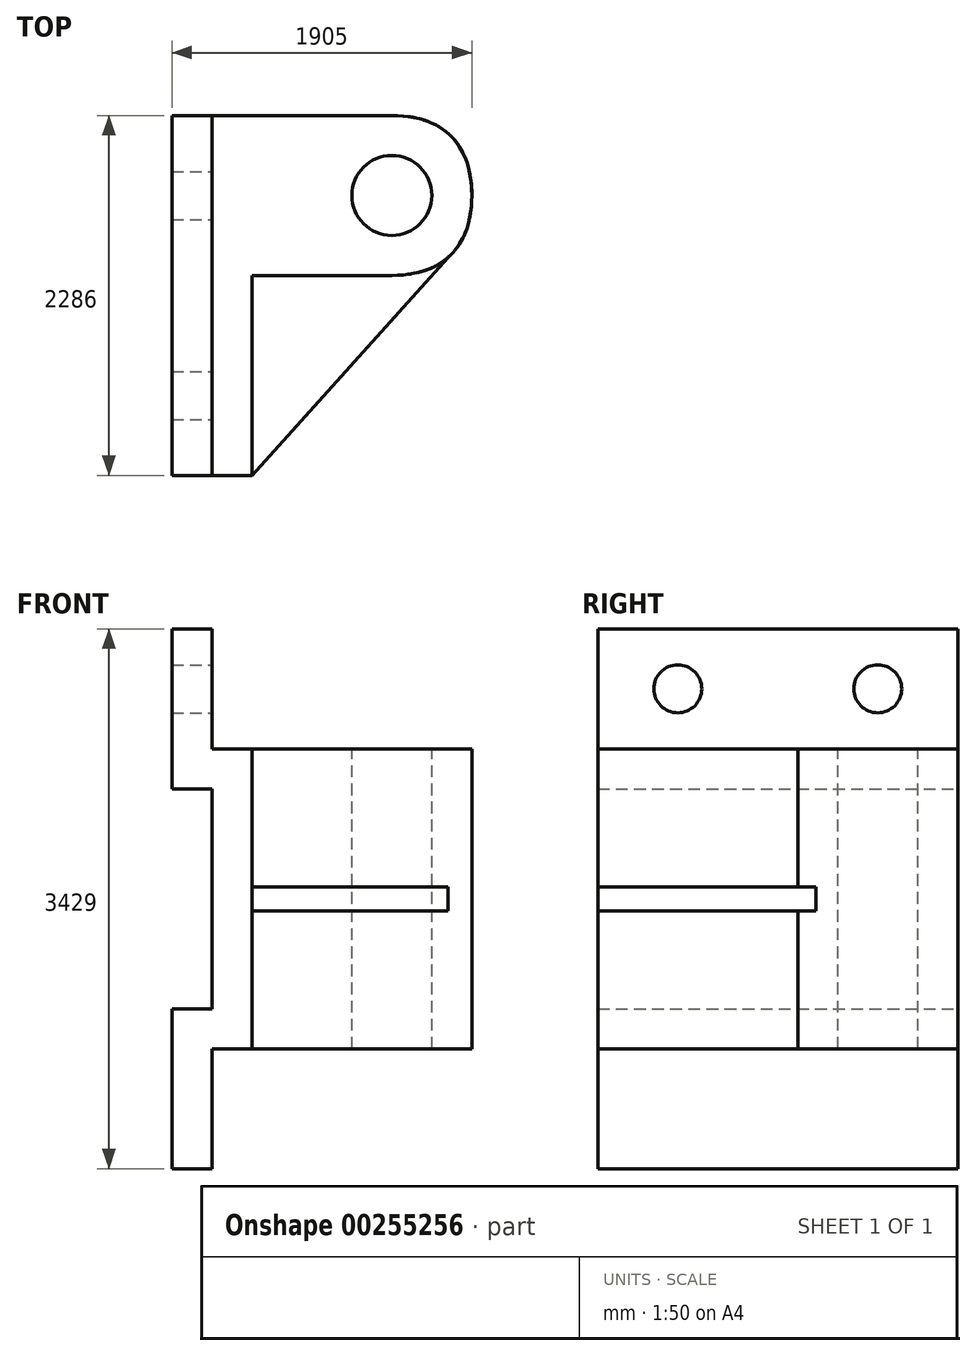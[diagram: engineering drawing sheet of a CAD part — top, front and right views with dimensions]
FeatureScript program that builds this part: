
annotation { "Feature Type Name" : "Feature", "Feature Type Description" : "" }
export const myFeature = defineFeature(function(context is Context, id is Id, definition is map)
    precondition{}
    {
        {
            var Q0;
            Q0=qCreatedBy(makeId("Front.planeOp"),FACE);
            var sketch = newSketch(context, id + "F0", { "sketchPlane" : qUnion([Q0])});
            skLineSegment(sketch, "E0.bottom", {"start": v(0, 0) * mm, "end": v(254, 0) * mm});
            skLineSegment(sketch, "E0.top", {"start": v(0, 1270) * mm, "end": v(254, 1270) * mm});
            skLineSegment(sketch, "E0.left", {"start": v(0, 0) * mm, "end": v(0, 1270) * mm});
            skLineSegment(sketch, "E0.right", {"start": v(254, 0) * mm, "end": v(254, 1270) * mm});
            skLineSegment(sketch, "E1", {"start": v(254, 0) * mm, "end": v(254, 762) * mm});
            skLineSegment(sketch, "E2.bottom", {"start": v(254, 762) * mm, "end": v(508, 762) * mm});
            skLineSegment(sketch, "E2.top", {"start": v(254, 2667) * mm, "end": v(508, 2667) * mm});
            skLineSegment(sketch, "E2.left", {"start": v(254, 762) * mm, "end": v(254, 2667) * mm});
            skLineSegment(sketch, "E2.right", {"start": v(508, 762) * mm, "end": v(508, 2667) * mm});
            skLineSegment(sketch, "E3", {"start": v(508, 1714.5) * mm, "end": v(749.87, 1714.5) * mm});
            skPoint(sketch, "E3.endSnap0", {"position": v(508, 1714.5) * mm});
            skLineSegment(sketch, "E4.MirrorCS", {"start": v(0, 2159) * mm, "end": v(254, 2159) * mm});
            skLineSegment(sketch, "E5.MirrorCS", {"start": v(0, 3429) * mm, "end": v(0, 2159) * mm});
            skLineSegment(sketch, "E6.MirrorCS", {"start": v(0, 3429) * mm, "end": v(254, 3429) * mm});
            skLineSegment(sketch, "E7.MirrorCS", {"start": v(254, 3429) * mm, "end": v(254, 2667) * mm});
            skSolve(sketch);
        }
        {
            var Q0;
            {var subQ0=sQuery(id+"F0.wireOp",EDGE,"E4.MirrorCS");Q0=makeQuery(id+"F0.imprint","IMPRINT",FACE,{"disambiguationData":[TD([[makeQuery(id+"F0.imprint","IMPRINT",EDGE,{"derivedFrom":subQ0}),1.0]])]});}
            var Q1;
            {var subQ3=sQuery(id+"F0.wireOp",EDGE,"E2.bottom");Q1=makeQuery(id+"F0.imprint","IMPRINT",FACE,{"disambiguationData":[TD([[makeQuery(id+"F0.imprint","IMPRINT",EDGE,{"derivedFrom":subQ3}),1.0]])]});}
            var Q2;
            Q2=makeQuery(id+"F0.imprint","IMPRINT",FACE,{"disambiguationData":[TD([[makeQuery(id+"F0.imprint","IMPRINT",EDGE,{"derivedFrom":sQuery(id+"F0.wireOp",EDGE,"E0.bottom")}),1.0]])]});
            extrude(context, id + "F1", {"entities" : qUnion([Q0, Q1, Q2]), "depth" : 2286 * mm});
        }
        {
            var Q0;
            Q0=makeQuery(id+"F1.opExtrude","SWEPT_FACE",FACE,{"disambiguationData":[OSD([sQuery(id+"F0.wireOp",EDGE,"E7.MirrorCS")])]});
            var sketch = newSketch(context, id + "F2", { "sketchPlane" : qUnion([Q0])});
            skLineSegment(sketch, "E8.bottom", {"start": v(-2286, 3429) * mm, "end": v(-1778, 3429) * mm});
            skLineSegment(sketch, "E8.top", {"start": v(-2286, 3048) * mm, "end": v(-1778, 3048) * mm});
            skLineSegment(sketch, "E8.left", {"start": v(-2286, 3429) * mm, "end": v(-2286, 3048) * mm});
            skLineSegment(sketch, "E8.right", {"start": v(-1778, 3429) * mm, "end": v(-1778, 3048) * mm});
            skCircle(sketch, "E9", {"center": v(-1778, 3048) * mm, "radius": 152.4 * mm});
            skLineSegment(sketch, "E10", {"start": v(-1778, 3048) * mm, "end": v(-508, 3048) * mm});
            skCircle(sketch, "E11", {"center": v(-508, 3048) * mm, "radius": 152.4 * mm});
            skLineSegment(sketch, "E12.0.0", {"start": v(0, 762) * mm, "end": v(0, 2667) * mm});
            skLineSegment(sketch, "E12.0.1", {"start": v(0, 2667) * mm, "end": v(-2286, 2667) * mm});
            skLineSegment(sketch, "E12.0.2", {"start": v(-2286, 2667) * mm, "end": v(-2286, 762) * mm});
            skLineSegment(sketch, "E12.0.3", {"start": v(-2286, 762) * mm, "end": v(0, 762) * mm});
            skLineSegment(sketch, "E13", {"start": v(-2286, 1714.5) * mm, "end": v(-1856.1, 1714.5) * mm});
            skCircle(sketch, "E14.MirrorC", {"center": v(-508, 381) * mm, "radius": 152.4 * mm});
            skCircle(sketch, "E15.MirrorC", {"center": v(-1778, 381) * mm, "radius": 152.4 * mm});
            skSolve(sketch);
        }
        {
            var Q0;
            {var subQ0=sQuery(id+"F2.wireOp",EDGE,"E10");var subQ3=sQuery(id+"F2.wireOp",EDGE,"E9");var subQ5=makeQuery(id+"F2.imprint","INTERSECT",VERTEX,{"derivedFrom":[subQ3,subQ0]});Q0=makeQuery(id+"F2.imprint","IMPRINT",FACE,{"disambiguationData":[TD([[makeQuery(id+"F2.imprint","IMPRINT",EDGE,{"disambiguationData":[TD([[subQ5,1.0]])],"derivedFrom":subQ3}),1.0]])]});}
            var Q1;
            {var subQ0=sQuery(id+"F2.wireOp",EDGE,"E10");var subQ3=sQuery(id+"F2.wireOp",EDGE,"E9");var subQ5=makeQuery(id+"F2.imprint","INTERSECT",VERTEX,{"derivedFrom":[subQ3,subQ0]});Q1=makeQuery(id+"F2.imprint","IMPRINT",FACE,{"disambiguationData":[TD([[makeQuery(id+"F2.imprint","IMPRINT",EDGE,{"disambiguationData":[TD([[subQ5,-1.0]])],"derivedFrom":subQ3}),1.0]])]});}
            var Q2;
            {var subQ1=sQuery(id+"F2.wireOp",EDGE,"E8.top");var subQ3=sQuery(id+"F2.wireOp",EDGE,"E9");var subQ4=makeQuery(id+"F2.imprint","INTERSECT",VERTEX,{"derivedFrom":[subQ1,subQ3]});Q2=makeQuery(id+"F2.imprint","IMPRINT",FACE,{"disambiguationData":[TD([[makeQuery(id+"F2.imprint","IMPRINT",EDGE,{"disambiguationData":[TD([[subQ4,1.0]])],"derivedFrom":subQ3}),1.0]])]});}
            var Q3;
            Q3=makeQuery(id+"F2.imprint","IMPRINT",FACE,{"disambiguationData":[TD([[makeQuery(id+"F2.imprint","IMPRINT",EDGE,{"derivedFrom":sQuery(id+"F2.wireOp",EDGE,"E11")}),1.0]])]});
            var Q4;
            Q4=makeQuery(id+"F2.imprint","IMPRINT",FACE,{"disambiguationData":[TD([[makeQuery(id+"F2.imprint","IMPRINT",EDGE,{"derivedFrom":sQuery(id+"F2.wireOp",EDGE,"E15.MirrorC")}),-1.0]])]});
            var Q5;
            Q5=makeQuery(id+"F2.imprint","IMPRINT",FACE,{"disambiguationData":[TD([[makeQuery(id+"F2.imprint","IMPRINT",EDGE,{"derivedFrom":sQuery(id+"F2.wireOp",EDGE,"E14.MirrorC")}),-1.0]])]});
            extrude(context, id + "F3", {"entities" : qUnion([Q0, Q1, Q2, Q3, Q4, Q5]), "operationType" : NewBodyOperationType.REMOVE, "oppositeDirection" : true, "depth" : 254 * mm});
        }
        {
            var Q0;
            Q0=makeQuery(id+"F1.opExtrude","SWEPT_FACE",FACE,{"disambiguationData":[OSD([sQuery(id+"F0.wireOp",EDGE,"E2.right")])]});
            var sketch = newSketch(context, id + "F4", { "sketchPlane" : qUnion([Q0])});
            skLineSegment(sketch, "E16.bottom", {"start": v(0, 2667) * mm, "end": v(-1016, 2667) * mm});
            skLineSegment(sketch, "E16.top", {"start": v(0, 762) * mm, "end": v(-1016, 762) * mm});
            skLineSegment(sketch, "E16.left", {"start": v(0, 2667) * mm, "end": v(0, 762) * mm});
            skLineSegment(sketch, "E16.right", {"start": v(-1016, 2667) * mm, "end": v(-1016, 762) * mm});
            skLineSegment(sketch, "E17", {"start": v(-2286, 1714.5) * mm, "end": v(-2286, 1790.7) * mm});
            skLineSegment(sketch, "E18.bottom", {"start": v(-2286, 1790.7) * mm, "end": v(-1016, 1790.7) * mm});
            skLineSegment(sketch, "E18.top", {"start": v(-2286, 1638.3) * mm, "end": v(-1016, 1638.3) * mm});
            skLineSegment(sketch, "E18.left", {"start": v(-2286, 1790.7) * mm, "end": v(-2286, 1638.3) * mm});
            skLineSegment(sketch, "E18.right", {"start": v(-1016, 1790.7) * mm, "end": v(-1016, 1638.3) * mm});
            skSolve(sketch);
        }
        {
            var Q0;
            {var subQ1=sQuery(id+"F4.wireOp",EDGE,"E16.bottom");Q0=makeQuery(id+"F4.imprint","IMPRINT",FACE,{"disambiguationData":[TD([[makeQuery(id+"F4.imprint","IMPRINT",EDGE,{"derivedFrom":subQ1}),-1.0]])]});}
            extrude(context, id + "F5", {"entities" : qUnion([Q0]), "operationType" : NewBodyOperationType.ADD, "depth" : 1397 * mm});
        }
        {
            var Q0;
            {var subQ0=sQuery(id+"F4.wireOp",EDGE,"E18.bottom");Q0=makeQuery(id+"F4.imprint","IMPRINT",FACE,{"disambiguationData":[TD([[makeQuery(id+"F4.imprint","IMPRINT",EDGE,{"derivedFrom":subQ0}),-1.0]])]});}
            extrude(context, id + "F6", {"entities" : qUnion([Q0]), "operationType" : NewBodyOperationType.ADD, "depth" : 1143 * mm});
        }
        {
            var Q0;
            Q0=makeQuery(id+"F6.opExtrude","CAP_EDGE",EDGE,{"disambiguationData":[OSD([sQuery(id+"F4.wireOp",EDGE,"E18.left")])],"isStart":false});
            chamfer(context, id + "F7", {"entities" : qUnion([Q0]), "chamferType" : ChamferType.TWO_OFFSETS, "width1" : 1143 * mm, "oppositeDirection" : false, "width2" : 1270 * mm, "tangentPropagation" : true});
        }
        {
            var Q0;
            Q0=makeQuery(id+"F5.opExtrude","CAP_EDGE",EDGE,{"disambiguationData":[OSD([sQuery(id+"F4.wireOp",EDGE,"E16.right"),sQuery(id+"F4.wireOp",EDGE,"E18.right")])],"isStart":false});
            var Q1;
            Q1=makeQuery(id+"F5.opExtrude","CAP_EDGE",EDGE,{"disambiguationData":[OSD([sQuery(id+"F4.wireOp",EDGE,"E16.left")])],"isStart":false});
            fillet(context, id + "F8", {"entities" : qUnion([Q0, Q1]), "radius" : 508 * mm, "tangentPropagation" : true, "rho" : .48, "crossSection" : FilletCrossSection.CONIC, "allowEdgeOverflow" : false});
        }
        {
            var Q0;
            Q0=makeQuery(id+"F5.boolean.opBoolean","MERGE",FACE,{"derivedFrom":[makeQuery(id+"F1.opExtrude","SWEPT_FACE",FACE,{"disambiguationData":[OSD([sQuery(id+"F0.wireOp",EDGE,"E2.top")])]}),makeQuery(id+"F5.opExtrude","SWEPT_FACE",FACE,{"disambiguationData":[OSD([sQuery(id+"F4.wireOp",EDGE,"E16.bottom")])]})]});
            var sketch = newSketch(context, id + "F9", { "sketchPlane" : qUnion([Q0])});
            skCircle(sketch, "E19", {"center": v(1397, -508) * mm, "radius": 508 * mm});
            skCircle(sketch, "E20", {"center": v(1397, -508) * mm, "radius": 254 * mm});
            skSolve(sketch);
        }
        {
            var Q0;
            Q0=makeQuery(id+"F9.imprint","IMPRINT",FACE,{"disambiguationData":[TD([[makeQuery(id+"F9.imprint","IMPRINT",EDGE,{"derivedFrom":sQuery(id+"F9.wireOp",EDGE,"E20")}),1.0]])]});
            extrude(context, id + "F10", {"entities" : qUnion([Q0]), "operationType" : NewBodyOperationType.REMOVE, "oppositeDirection" : true, "depth" : 2540 * mm});
        }
        {
            var Q0;
            Q0=makeQuery(id+"F1.opExtrude","SWEPT_FACE",FACE,{"disambiguationData":[OSD([sQuery(id+"F0.wireOp",EDGE,"E4.MirrorCS")])]});
            var sketch = newSketch(context, id + "F11", { "sketchPlane" : qUnion([Q0])});
            skLineSegment(sketch, "E21.bottom", {"start": v(0, 2286) * mm, "end": v(254, 2286) * mm});
            skLineSegment(sketch, "E21.top", {"start": v(0, 0) * mm, "end": v(254, 0) * mm});
            skLineSegment(sketch, "E21.left", {"start": v(0, 2286) * mm, "end": v(0, 0) * mm});
            skLineSegment(sketch, "E21.right", {"start": v(254, 2286) * mm, "end": v(254, 0) * mm});
            skSolve(sketch);
        }
        {
            var Q0;
            Q0=makeQuery(id+"F11.imprint","IMPRINT",FACE,{"disambiguationData":[TD([[makeQuery(id+"F11.imprint","IMPRINT",EDGE,{"derivedFrom":sQuery(id+"F11.wireOp",EDGE,"E21.bottom")}),-1.0]])]});
            extrude(context, id + "F12", {"entities" : qUnion([Q0]), "operationType" : NewBodyOperationType.REMOVE, "oppositeDirection" : true, "depth" : 254 * mm, "hasSecondDirection" : true, "secondDirectionOppositeDirection" : false, "secondDirectionDepth" : 1143 * mm});
        }
    });
